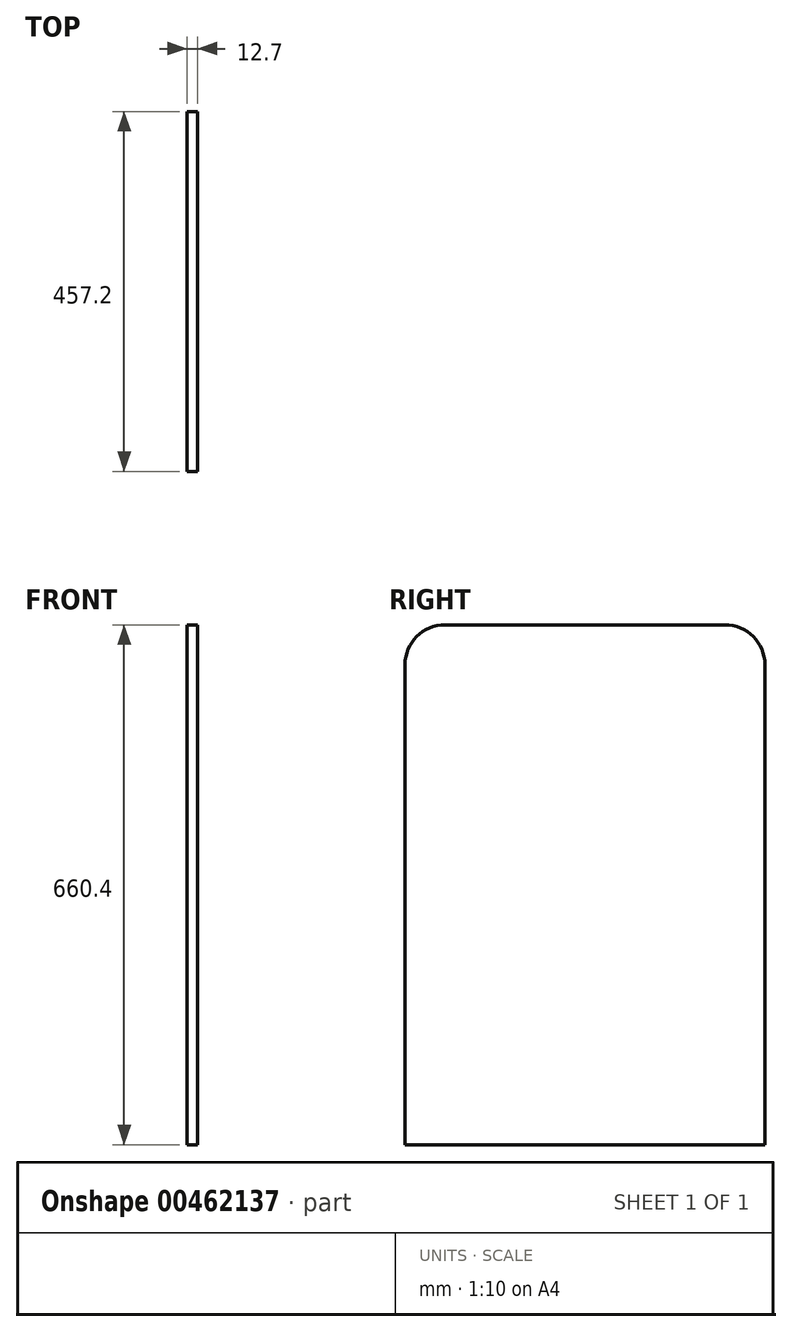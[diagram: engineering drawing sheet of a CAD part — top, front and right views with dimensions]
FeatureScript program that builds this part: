
annotation { "Feature Type Name" : "Feature", "Feature Type Description" : "" }
export const myFeature = defineFeature(function(context is Context, id is Id, definition is map)
    precondition{}
    {
        {
            var Q0;
            Q0=qCreatedBy(makeId("Right.planeOp"),FACE);
            var sketch = newSketch(context, id + "F0", { "sketchPlane" : qUnion([Q0])});
            skLineSegment(sketch, "E0.bottom", {"start": v(0, 0) * mm, "end": v(457.2, 0) * mm});
            skLineSegment(sketch, "E0.top", {"start": v(0, 660.4) * mm, "end": v(457.2, 660.4) * mm});
            skLineSegment(sketch, "E0.left", {"start": v(0, 0) * mm, "end": v(0, 660.4) * mm});
            skLineSegment(sketch, "E0.right", {"start": v(457.2, 0) * mm, "end": v(457.2, 660.4) * mm});
            skSolve(sketch);
        }
        {
            var Q0;
            Q0 = qSketchRegion(id + "F0", true);
            extrude(context, id + "F1", {"entities" : qUnion([Q0]), "depth" : 12.7 * mm});
        }
        {
            var Q0;
            Q0=makeQuery(id+"F1.opExtrude","SWEPT_EDGE",EDGE,{"disambiguationData":[OSD([sQuery(id+"F0.wireOp",EDGE,"E0.top"),sQuery(id+"F0.wireOp",EDGE,"E0.left")])]});
            var Q1;
            Q1=makeQuery(id+"F1.opExtrude","SWEPT_EDGE",EDGE,{"disambiguationData":[OSD([sQuery(id+"F0.wireOp",EDGE,"E0.top"),sQuery(id+"F0.wireOp",EDGE,"E0.right")])]});
            fillet(context, id + "F2", {"entities" : qUnion([Q0, Q1]), "radius" : 50.8 * mm, "tangentPropagation" : true, "allowEdgeOverflow" : false});
        }
    });
